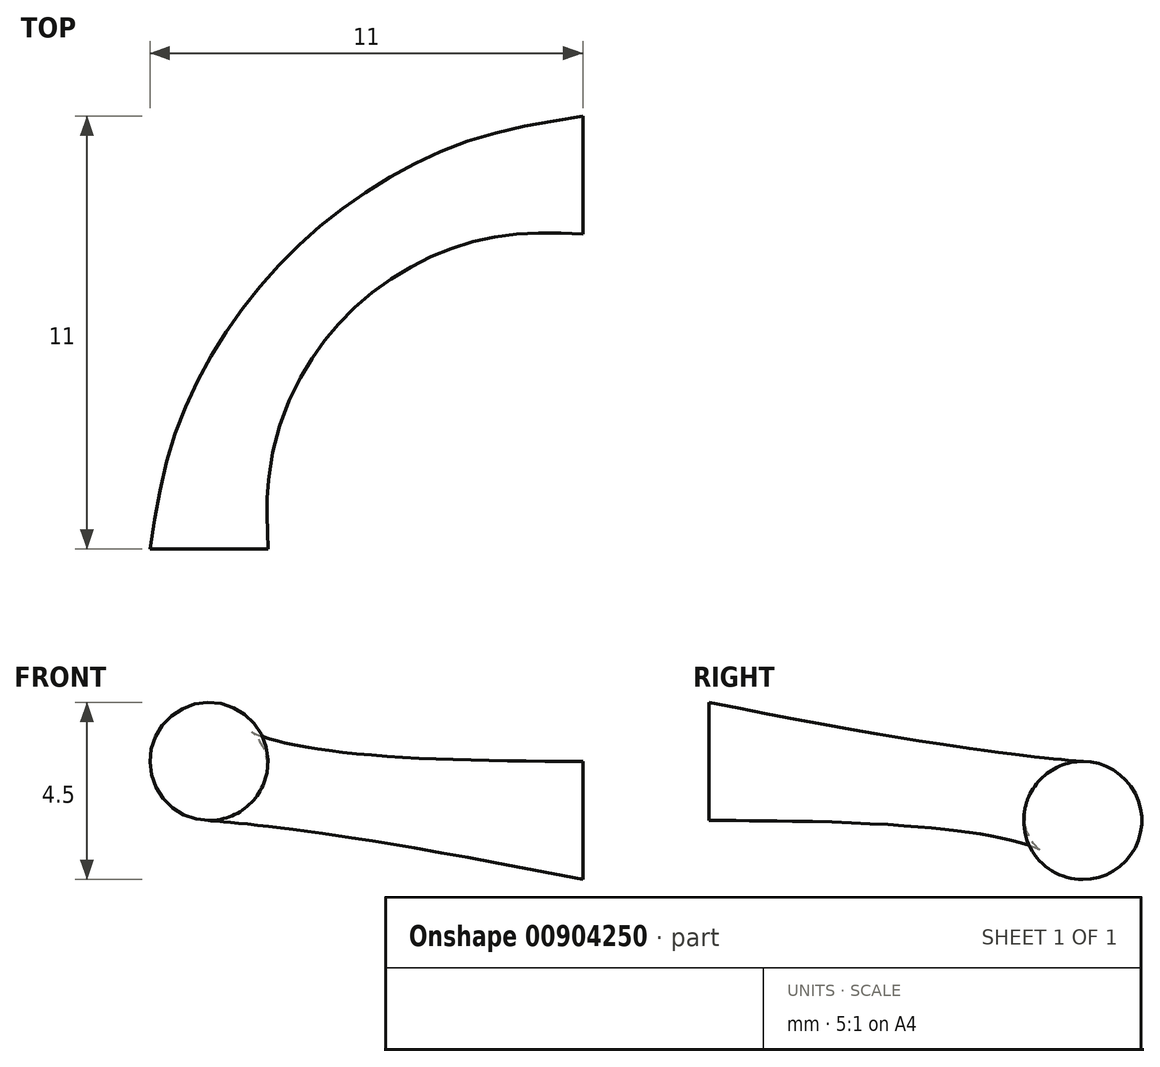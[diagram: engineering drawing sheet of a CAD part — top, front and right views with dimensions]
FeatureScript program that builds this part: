
annotation { "Feature Type Name" : "Feature", "Feature Type Description" : "" }
export const myFeature = defineFeature(function(context is Context, id is Id, definition is map)
    precondition{}
    {
        {
            var Q0;
            Q0=qCreatedBy(makeId("Front.planeOp"),FACE);
            var sketch = newSketch(context, id + "F0", { "sketchPlane" : qUnion([Q0])});
            skLineSegment(sketch, "E0", {"start": v(0, 0) * mm, "end": v(-8, 0) * mm});
            skLineSegment(sketch, "E1", {"start": v(-8, 0) * mm, "end": v(-9.5, 0) * mm});
            skCircle(sketch, "E2", {"center": v(-9.5, 0) * mm, "radius": 1.5 * mm});
            skSolve(sketch);
        }
        {
            var Q0;
            Q0=qCreatedBy(makeId("Right.planeOp"),FACE);
            var sketch = newSketch(context, id + "F1", { "sketchPlane" : qUnion([Q0])});
            skLineSegment(sketch, "E3", {"start": v(0, 0) * mm, "end": v(0, -1.5) * mm});
            skLineSegment(sketch, "E4", {"start": v(0, -1.5) * mm, "end": v(8, -1.5) * mm});
            skLineSegment(sketch, "E5", {"start": v(8, -1.5) * mm, "end": v(9.5, -1.5) * mm});
            skCircle(sketch, "E6", {"center": v(9.5, -1.5) * mm, "radius": 1.5 * mm});
            skSolve(sketch);
        }
        {
            var Q0;
            Q0=makeQuery(id+"F1.imprint","IMPRINT",FACE,{"disambiguationData":[TD([[makeQuery(id+"F1.imprint","IMPRINT",EDGE,{"derivedFrom":sQuery(id+"F1.wireOp",EDGE,"E6")}),1.0]])]});
            extrude(context, id + "F2", {"entities" : qUnion([Q0]), "depth" : 1 * mm, "offsetDistance" : 25 * mm});
        }
        {
            var Q0;
            Q0=makeQuery(id+"F0.imprint","IMPRINT",FACE,{"disambiguationData":[TD([[makeQuery(id+"F0.imprint","IMPRINT",EDGE,{"derivedFrom":sQuery(id+"F0.wireOp",EDGE,"E2")}),1.0]])]});
            extrude(context, id + "F3", {"entities" : qUnion([Q0]), "depth" : 1 * mm, "offsetDistance" : 25 * mm});
        }
        {
            var Q0;
            Q0=qCreatedBy(makeId("Top.planeOp"),FACE);
            var sketch = newSketch(context, id + "F4", { "sketchPlane" : qUnion([Q0])});
            skPoint(sketch, "E7.0", {"position": v(0, 9.5) * mm});
            skPoint(sketch, "E8.0", {"position": v(-9.5, 0) * mm});
            skLineSegment(sketch, "E9", {"start": v(-9.5, 0) * mm, "end": v(-9.5, -2.62) * mm});
            skLineSegment(sketch, "E10", {"start": v(0, 9.5) * mm, "end": v(3.15, 9.5) * mm});
            skArc(sketch, "E11", {"start": v(0, 9.5) * mm, "mid": v(-6.72, 6.72) * mm, "end": v(-9.5, 0) * mm});
            skSolve(sketch);
        }
        {
            var Q0;
            Q0=sQuery(id+"F4.wireOp",EDGE,"E11");
            var Q2;
            Q2=makeQuery(id+"F0.imprint","IMPRINT",FACE,{"disambiguationData":[TD([[makeQuery(id+"F0.imprint","IMPRINT",EDGE,{"derivedFrom":sQuery(id+"F0.wireOp",EDGE,"E2")}),1.0]])]});
            var Q3;
            Q3=makeQuery(id+"F1.imprint","IMPRINT",FACE,{"disambiguationData":[TD([[makeQuery(id+"F1.imprint","IMPRINT",EDGE,{"derivedFrom":sQuery(id+"F1.wireOp",EDGE,"E6")}),1.0]])]});
            loft(context, id + "F5", {"operationType" : NewBodyOperationType.ADD, "addSections" : true, "spine" : qUnion([Q0]), "sectionCount" : 5, "sheetProfilesArray" : [{ "sheetProfileEntities" : qUnion([Q2]) }, { "sheetProfileEntities" : qUnion([Q3]) }]});
        }
        {
            var Q0;
            Q0=makeQuery(id+"F3.opExtrude","CAP_FACE",FACE,{"disambiguationData":[OSD([sQuery(id+"F0.wireOp",EDGE,"E2")])],"isStart":false});
            extrude(context, id + "F6", {"entities" : qUnion([Q0]), "operationType" : NewBodyOperationType.REMOVE, "oppositeDirection" : true, "depth" : 1 * mm, "offsetDistance" : 25 * mm});
        }
        {
            var Q0;
            Q0=makeQuery(id+"F2.opExtrude","CAP_FACE",FACE,{"disambiguationData":[OSD([sQuery(id+"F1.wireOp",EDGE,"E6")])],"isStart":false});
            extrude(context, id + "F7", {"entities" : qUnion([Q0]), "operationType" : NewBodyOperationType.REMOVE, "oppositeDirection" : true, "depth" : 1 * mm, "offsetDistance" : 25 * mm});
        }
    });
